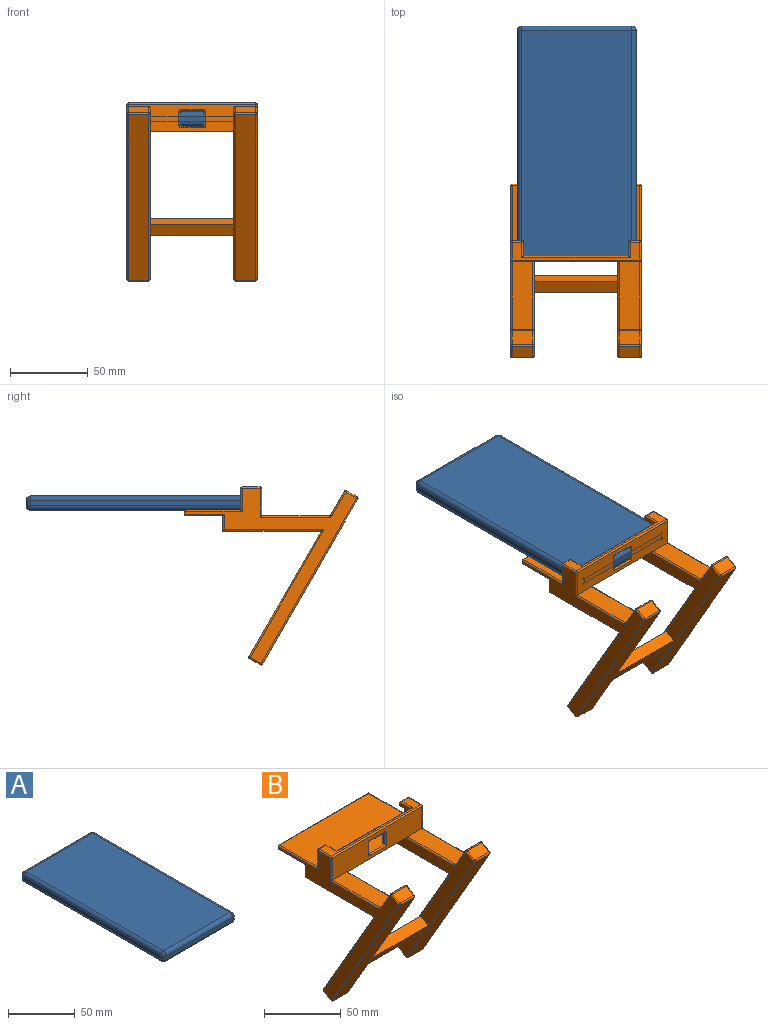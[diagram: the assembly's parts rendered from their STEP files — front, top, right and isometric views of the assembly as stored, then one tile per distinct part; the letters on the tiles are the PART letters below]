
ASSEMBLY  parts=2 mates=1
PART A: 26 faces, bbox 76.8x151.9x9.2 mm
  f0: plane 70.77x3.23mm, normal (0,1,0), area 228.6mm2, adj f14,f19,f22,f25
  f1: plane 145.85x3.23mm, normal (-1,0,0), area 471.1mm2, adj f11,f20,f21,f25
  f2: plane 70.77x3.23mm, normal (0,-1,0), area 228.6mm2, adj f6,f10,f11,f12
  f3: plane 145.85x3.23mm, normal (1,0,0), area 471.1mm2, adj f6,f9,f13,f14
  f4: plane 145.85x70.77mm, normal (0,0,1), area 10321.8mm2, adj f9,f10,f19,f20
  f5: plane 145.85x70.77mm, normal (0,0,-1), area 10321.8mm2, adj f12,f13,f21,f22
  f6: cylinder r=3mm len=3.23mm, axis (0,0,1), area 15.2mm2, adj f2,f3,f7,f8
  f7: sphere r=3mm, area 14.1mm2, adj f6,f9,f10
  f8: sphere r=3mm, area 14.1mm2, adj f6,f12,f13
  f9: cylinder r=3mm len=145.85mm, axis (0,-1,0), area 687.3mm2, adj f3,f4,f7,f15
  f10: cylinder r=3mm len=70.77mm, axis (-1,0,0), area 333.5mm2, adj f2,f4,f7,f16
  f11: cylinder r=3mm len=3.23mm, axis (0,0,-1), area 15.2mm2, adj f1,f2,f16,f17
  f12: cylinder r=3mm len=70.77mm, axis (1,0,0), area 333.5mm2, adj f2,f5,f8,f17
  f13: cylinder r=3mm len=145.85mm, axis (0,1,0), area 687.3mm2, adj f3,f5,f8,f18
  f14: cylinder r=3mm len=3.23mm, axis (0,0,-1), area 15.2mm2, adj f0,f3,f15,f18
  f15: sphere r=3mm, area 14.1mm2, adj f9,f14,f19
  f16: sphere r=3mm, area 14.1mm2, adj f10,f11,f20
  f17: sphere r=3mm, area 14.1mm2, adj f11,f12,f21
  f18: sphere r=3mm, area 14.1mm2, adj f13,f14,f22
  f19: cylinder r=3mm len=70.77mm, axis (1,0,0), area 333.5mm2, adj f0,f4,f15,f23
  f20: cylinder r=3mm len=145.85mm, axis (0,1,0), area 687.3mm2, adj f1,f4,f16,f23
  f21: cylinder r=3mm len=145.85mm, axis (0,-1,0), area 687.3mm2, adj f1,f5,f17,f24
  f22: cylinder r=3mm len=70.77mm, axis (-1,0,0), area 333.5mm2, adj f0,f5,f18,f24
  f23: sphere r=3mm, area 14.1mm2, adj f19,f20,f25
  f24: sphere r=3mm, area 14.1mm2, adj f21,f22,f25
  f25: cylinder r=3mm len=3.23mm, axis (0,0,1), area 15.2mm2, adj f0,f1,f23,f24
PART B: 140 faces, bbox 84x112.1x114.7 mm
  f0: plane 32.22x23.22mm, normal (-1,0,0), area 260.7mm2, adj f82,f89,f109,f139
  f1: plane 32.22x23.22mm, normal (1,0,0), area 260.7mm2, adj f54,f61,f106,f139
  f2: plane 86.13x75.37mm, normal (1,0,0), area 1224.5mm2, adj f3,f6,f33,f47,f54,f102,f103,f104
  f3: plane 82x49mm, normal (0,0,-1), area 3318mm2, adj f2,f6,f24,f25,f33,f59,f88,f112
  f4: plane 82x48mm, normal (0,0,1), area 3685.1mm2, adj f5,f12,f14,f17,f19,f21,f52,f81
  f5: plane 77x14mm, normal (0,1,0), area 840.2mm2, adj f4,f14,f15,f16,f18,f19,f20,f116
  f6: plane 82x18.5mm, normal (0,-1,0), area 1234mm2, adj f2,f3,f23,f25,f32,f42,f71,f100
  f7: plane 82x1.5mm, normal (0,1,0), area 123mm2, adj f55,f84,f111,f112
  f8: plane 112.74x110.13mm, normal (-1,0,0), area 1806.7mm2, adj f40,f41,f42,f43,f45,f48,f49,f52
  f9: plane 112.74x110.13mm, normal (1,0,0), area 1806.7mm2, adj f69,f70,f71,f73,f74,f77,f80,f81
  f10: plane 82x11.5mm, normal (0,0,1), area 243mm2, adj f45,f74,f113,f114,f115,f116,f117,f118
  f11: plane 8x1.5mm, normal (1,0,0), area 12mm2, adj f122,f123,f130,f131
  f12: plane 9x1.5mm, normal (-1,0,0), area 13.5mm2, adj f4,f120,f128,f134
  f13: plane 13x1.5mm, normal (0,0,-1), area 19.5mm2, adj f121,f122,f128,f129
  f14: plane 11.5x10mm, normal (-1,0,0), area 115mm2, adj f4,f5,f15,f17
  f15: plane 10x4.5mm, normal (0,0,-1), area 45mm2, adj f5,f14,f16,f17
  f16: plane 10x2.5mm, normal (-1,0,0), area 25mm2, adj f5,f15,f17,f115
  f17: plane 14x7mm, normal (0,1,0), area 46.3mm2, adj f4,f14,f15,f16,f77,f114
  f18: plane 10x4.5mm, normal (0,0,-1), area 45mm2, adj f5,f19,f20,f21
  f19: plane 11.5x10mm, normal (1,0,0), area 114.8mm2, adj f4,f5,f18,f21,f124
  f20: plane 10x2.5mm, normal (1,0,0), area 25mm2, adj f5,f18,f21,f117
  f21: plane 14x7mm, normal (0,1,0), area 46.3mm2, adj f4,f18,f19,f20,f48,f118
  f22: plane 63.45x13mm, normal (0,0,-1), area 824.9mm2, adj f24,f28,f94,f108
  f23: plane 43.65x13mm, normal (0,0,1), area 567.4mm2, adj f6,f68,f69,f100
  f24: plane 14x10mm, normal (0,1,0), area 139.8mm2, adj f3,f22,f25,f91,f108
  f25: plane 86.13x75.37mm, normal (-1,0,0), area 1224.5mm2, adj f3,f6,f24,f75,f82,f98,f99,f100
  f26: plane 15.28x13mm, normal (0,0.87,0.5), area 229.4mm2, adj f68,f72,f73,f98
  f27: plane 106.52x61.5mm, normal (0,-0.87,-0.5), area 1599mm2, adj f79,f82,f86,f87
  f28: plane 80.74x46.61mm, normal (0,0.87,0.5), area 1211.9mm2, adj f22,f92,f96,f109
  f29: plane 13x6.93mm, normal (0,-0.5,0.87), area 104mm2, adj f72,f75,f79,f80
  f30: plane 13x6.93mm, normal (0,0.5,-0.87), area 104mm2, adj f86,f89,f92,f93
  f31: plane 63.45x13mm, normal (0,0,-1), area 824.9mm2, adj f33,f36,f65,f105
  f32: plane 43.65x13mm, normal (0,0,1), area 567.4mm2, adj f6,f39,f40,f104
  f33: plane 14x10mm, normal (0,1,0), area 139.8mm2, adj f2,f3,f31,f62,f105
  f34: plane 15.28x13mm, normal (0,0.87,0.5), area 229.4mm2, adj f39,f43,f44,f102
  f35: plane 106.52x61.5mm, normal (0,-0.87,-0.5), area 1599mm2, adj f50,f54,f56,f57
  f36: plane 80.74x46.61mm, normal (0,0.87,0.5), area 1211.9mm2, adj f31,f64,f67,f106
  f37: plane 13x6.93mm, normal (0,-0.5,0.87), area 104mm2, adj f44,f47,f49,f50
  f38: plane 13x6.93mm, normal (0,0.5,-0.87), area 104mm2, adj f57,f61,f63,f64
  f39: cylinder r=1mm len=13mm, axis (-1,0,0), area 13.6mm2, adj f32,f34,f41,f103
  f40: cylinder r=1mm len=44.65mm, axis (0,-1,0), area 69.1mm2, adj f8,f32,f41,f42
  f41: torus R=2mm, axis (1,0,0), area 2.2mm2, adj f8,f39,f40,f43
  f42: cylinder r=1mm len=19.21mm, axis (0,0,-1), area 28.6mm2, adj f6,f8,f40,f45,f113
  f43: cylinder r=1mm len=15.78mm, axis (0,0.5,-0.87), area 27.7mm2, adj f8,f34,f41,f46
  f44: cylinder r=1mm len=13mm, axis (-1,0,0), area 20.4mm2, adj f34,f37,f46,f101
  f45: cylinder r=1mm len=12.91mm, axis (0,1,0), area 19.2mm2, adj f8,f10,f42,f48,f113,f118
  f46: sphere r=1mm, area 1.6mm2, adj f43,f44,f49
  f47: cylinder r=1mm len=7.43mm, axis (0,0.87,0.5), area 12.6mm2, adj f2,f37,f51,f101
  f48: cylinder r=1mm len=15.71mm, axis (0,0,1), area 23.1mm2, adj f8,f21,f45,f52,f118
  f49: cylinder r=1mm len=7.43mm, axis (0,0.87,0.5), area 12.6mm2, adj f8,f37,f46,f53
  f50: cylinder r=1mm len=13mm, axis (1,0,0), area 20.4mm2, adj f35,f37,f51,f53
  f51: sphere r=1mm, area 1.6mm2, adj f47,f50,f54
  f52: cylinder r=1mm len=37.21mm, axis (0,1,0), area 56.9mm2, adj f4,f8,f48,f55,f111
  f53: sphere r=1mm, area 1.6mm2, adj f49,f50,f56
  f54: cylinder r=1mm len=107.02mm, axis (0,-0.5,0.87), area 193.2mm2, adj f1,f2,f35,f51,f58,f138
  f55: cylinder r=1mm len=2.91mm, axis (0,0,1), area 3.5mm2, adj f7,f8,f52,f59,f111,f112
  f56: cylinder r=1mm len=107.02mm, axis (0,-0.5,0.87), area 193.2mm2, adj f8,f35,f53,f60
  f57: cylinder r=1mm len=13mm, axis (-1,0,0), area 20.4mm2, adj f35,f38,f58,f60
  f58: sphere r=1mm, area 1.6mm2, adj f54,f57,f61
  f59: cylinder r=1mm len=25.71mm, axis (0,-1,0), area 38.9mm2, adj f3,f8,f55,f62,f112
  f60: sphere r=1mm, area 1.6mm2, adj f56,f57,f63
  f61: cylinder r=1mm len=7.43mm, axis (0,-0.87,-0.5), area 12.6mm2, adj f1,f38,f58,f107
  f62: cylinder r=1mm len=11mm, axis (0,0,-1), area 15.7mm2, adj f8,f33,f59,f65
  f63: cylinder r=1mm len=7.43mm, axis (0,-0.87,-0.5), area 12.6mm2, adj f8,f38,f60,f66
  f64: cylinder r=1mm len=13mm, axis (1,0,0), area 20.4mm2, adj f36,f38,f66,f107
  f65: cylinder r=1mm len=65.19mm, axis (0,1,0), area 100.1mm2, adj f8,f31,f62,f67
  f66: sphere r=1mm, area 1.6mm2, adj f63,f64,f67
  f67: cylinder r=1mm len=82.74mm, axis (0,0.5,-0.87), area 147.4mm2, adj f8,f36,f65,f66
  f68: cylinder r=1mm len=13mm, axis (1,0,0), area 13.6mm2, adj f23,f26,f70,f99
  f69: cylinder r=1mm len=44.65mm, axis (0,1,0), area 69.1mm2, adj f9,f23,f70,f71
  f70: torus R=2mm, axis (1,0,0), area 2.2mm2, adj f9,f68,f69,f73
  f71: cylinder r=1mm len=19.21mm, axis (0,0,1), area 28.6mm2, adj f6,f9,f69,f74,f113
  f72: cylinder r=1mm len=13mm, axis (1,0,0), area 20.4mm2, adj f26,f29,f76,f97
  f73: cylinder r=1mm len=15.78mm, axis (0,-0.5,0.87), area 27.7mm2, adj f9,f26,f70,f76
  f74: cylinder r=1mm len=12.91mm, axis (0,-1,0), area 19.2mm2, adj f9,f10,f71,f77,f113,f114
  f75: cylinder r=1mm len=7.43mm, axis (0,0.87,0.5), area 12.6mm2, adj f25,f29,f78,f97
  f76: sphere r=1mm, area 1.6mm2, adj f72,f73,f80
  f77: cylinder r=1mm len=15.71mm, axis (0,0,-1), area 23.1mm2, adj f9,f17,f74,f81,f114
  f78: sphere r=1mm, area 1.6mm2, adj f75,f79,f82
  f79: cylinder r=1mm len=13mm, axis (-1,0,0), area 20.4mm2, adj f27,f29,f78,f83
  f80: cylinder r=1mm len=7.43mm, axis (0,-0.87,-0.5), area 12.6mm2, adj f9,f29,f76,f83
  f81: cylinder r=1mm len=37.21mm, axis (0,-1,0), area 56.9mm2, adj f4,f9,f77,f84,f111
  f82: cylinder r=1mm len=107.02mm, axis (0,-0.5,0.87), area 193.2mm2, adj f0,f25,f27,f78,f85,f138
  f83: sphere r=1mm, area 1.6mm2, adj f79,f80,f87
  f84: cylinder r=1mm len=2.91mm, axis (0,0,-1), area 3.5mm2, adj f7,f9,f81,f88,f111,f112
  f85: sphere r=1mm, area 1.6mm2, adj f82,f86,f89
  f86: cylinder r=1mm len=13mm, axis (1,0,0), area 20.4mm2, adj f27,f30,f85,f90
  f87: cylinder r=1mm len=107.02mm, axis (0,0.5,-0.87), area 193.2mm2, adj f9,f27,f83,f90
  f88: cylinder r=1mm len=25.71mm, axis (0,1,0), area 38.9mm2, adj f3,f9,f84,f91,f112
  f89: cylinder r=1mm len=7.43mm, axis (0,-0.87,-0.5), area 12.6mm2, adj f0,f30,f85,f110
  f90: sphere r=1mm, area 1.6mm2, adj f86,f87,f93
  f91: cylinder r=1mm len=11mm, axis (0,0,1), area 15.7mm2, adj f9,f24,f88,f94
  f92: cylinder r=1mm len=13mm, axis (-1,0,0), area 20.4mm2, adj f28,f30,f95,f110
  f93: cylinder r=1mm len=7.43mm, axis (0,0.87,0.5), area 12.6mm2, adj f9,f30,f90,f95
  f94: cylinder r=1mm len=65.19mm, axis (0,-1,0), area 100.1mm2, adj f9,f22,f91,f96
  f95: sphere r=1mm, area 1.6mm2, adj f92,f93,f96
  f96: cylinder r=1mm len=82.74mm, axis (0,-0.5,0.87), area 147.4mm2, adj f9,f28,f94,f95
  f97: sphere r=1mm, area 1.6mm2, adj f72,f75,f98
  f98: cylinder r=1mm len=15.78mm, axis (0,0.5,-0.87), area 27.7mm2, adj f25,f26,f97,f99
  f99: torus R=2mm, axis (1,0,0), area 2.2mm2, adj f25,f68,f98,f100
  f100: cylinder r=1mm len=43.65mm, axis (0,1,0), area 68.6mm2, adj f6,f23,f25,f99
  f101: sphere r=1mm, area 1.6mm2, adj f44,f47,f102
  f102: cylinder r=1mm len=15.78mm, axis (0,0.5,-0.87), area 27.7mm2, adj f2,f34,f101,f103
  f103: torus R=2mm, axis (-1,0,0), area 2.2mm2, adj f2,f39,f102,f104
  f104: cylinder r=1mm len=43.65mm, axis (0,1,0), area 68.6mm2, adj f2,f6,f32,f103
  f105: cylinder r=1mm len=65.19mm, axis (0,-1,0), area 100.7mm2, adj f2,f31,f33,f106
  f106: cylinder r=1mm len=82.74mm, axis (0,0.5,-0.87), area 147.4mm2, adj f1,f2,f36,f105,f107,f136
  f107: sphere r=1mm, area 1.6mm2, adj f61,f64,f106
  f108: cylinder r=1mm len=65.19mm, axis (0,-1,0), area 100.7mm2, adj f22,f24,f25,f109
  f109: cylinder r=1mm len=82.74mm, axis (0,0.5,-0.87), area 147.4mm2, adj f0,f25,f28,f108,f110,f136
  f110: sphere r=1mm, area 1.6mm2, adj f89,f92,f109
  f111: cylinder r=1mm len=83.41mm, axis (1,0,0), area 130mm2, adj f4,f7,f52,f55,f81,f84
  f112: cylinder r=1mm len=83.41mm, axis (-1,0,0), area 130mm2, adj f3,f7,f55,f59,f84,f88
  f113: cylinder r=1mm len=83.41mm, axis (-1,0,0), area 130mm2, adj f6,f10,f42,f45,f71,f74
  f114: cylinder r=1mm len=7.71mm, axis (1,0,0), area 11mm2, adj f10,f17,f74,f77,f115
  f115: cylinder r=1mm len=11mm, axis (0,-1,0), area 15.7mm2, adj f10,f16,f114,f116
  f116: cylinder r=1mm len=70mm, axis (1,0,0), area 108mm2, adj f5,f10,f115,f117
  f117: cylinder r=1mm len=11mm, axis (0,1,0), area 15.7mm2, adj f10,f20,f116,f118
  f118: cylinder r=1mm len=7.71mm, axis (1,0,0), area 11mm2, adj f10,f21,f45,f48,f117
  f119: torus R=2mm, axis (0,1,0), area 3.4mm2, adj f5,f121,f122,f123
  f120: cylinder r=1mm len=9mm, axis (0,0,1), area 14.1mm2, adj f4,f5,f12,f125
  f121: cylinder r=1mm len=13mm, axis (-1,0,0), area 20.4mm2, adj f5,f13,f119,f125
  f122: cylinder r=1mm len=1.5mm, axis (0,-1,0), area 2.4mm2, adj f11,f13,f119,f126
  f123: cylinder r=1mm len=8mm, axis (0,0,-1), area 12.6mm2, adj f5,f11,f119,f127
  f124: cylinder r=1mm len=30mm, axis (-1,0,0), area 47.1mm2, adj f4,f5,f19,f127
  f125: torus R=2mm, axis (0,1,0), area 3.4mm2, adj f5,f120,f121,f128
  f126: torus R=2mm, axis (0,1,0), area 3.4mm2, adj f6,f122,f129,f130
  f127: torus R=2mm, axis (0,0,1), area 3.4mm2, adj f4,f123,f124,f131
  f128: cylinder r=1mm len=1.5mm, axis (0,1,0), area 2.4mm2, adj f12,f13,f125,f132
  f129: cylinder r=1mm len=13mm, axis (1,0,0), area 20.4mm2, adj f6,f13,f126,f132
  f130: cylinder r=1mm len=8mm, axis (0,0,1), area 12.6mm2, adj f6,f11,f126,f133
  f131: cylinder r=1mm len=1.5mm, axis (0,1,0), area 2.4mm2, adj f4,f11,f127,f133
  f132: torus R=2mm, axis (0,1,0), area 3.4mm2, adj f6,f128,f129,f134
  f133: torus R=2mm, axis (0,1,0), area 3.4mm2, adj f6,f130,f131,f135
  f134: cylinder r=1mm len=10mm, axis (0,0,-1), area 14.7mm2, adj f6,f12,f132,f135
  f135: cylinder r=1mm len=15mm, axis (-1,0,0), area 22.6mm2, adj f4,f6,f133,f134
  f136: plane 54x6.93mm, normal (0,0.87,0.5), area 432mm2, adj f106,f109,f137,f139
  f137: plane 54x6.93mm, normal (0,-0.5,0.87), area 432mm2, adj f2,f25,f136,f138
  f138: plane 54x6.93mm, normal (0,-0.87,-0.5), area 432mm2, adj f54,f82,f137,f139
  f139: plane 54x6.93mm, normal (0,0.5,-0.87), area 432mm2, adj f0,f1,f136,f138
PLACE A t=(-16.53,45.22,-1.51)mm
PLACE B t=(-20.59,-56.63,-5.01)mm
MATE planar B.f4 <-> A.f5  axis (0,0,1) through (21.61,-80.18,-1.51)mm
